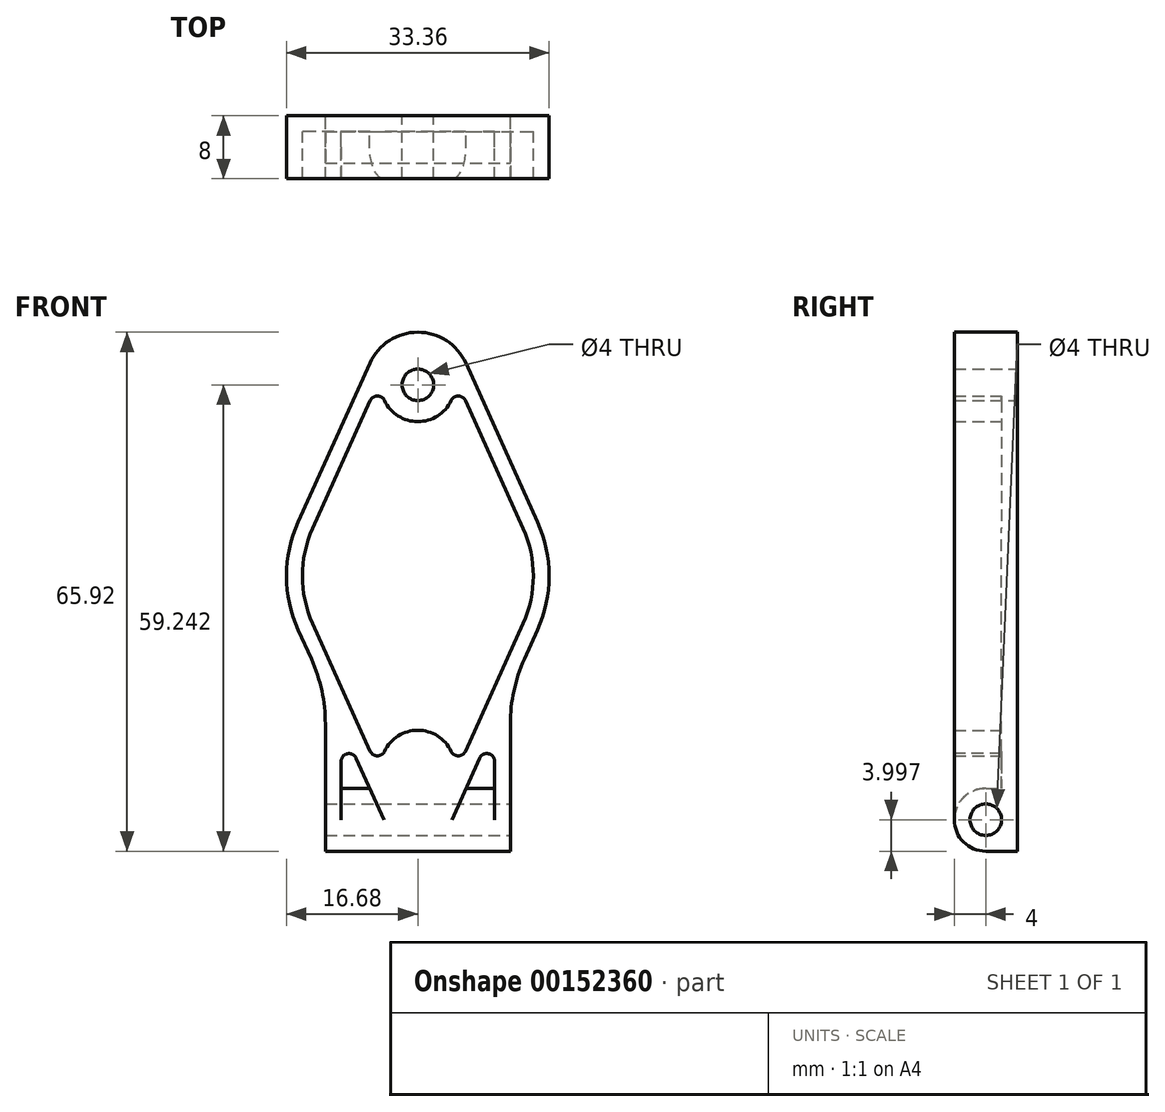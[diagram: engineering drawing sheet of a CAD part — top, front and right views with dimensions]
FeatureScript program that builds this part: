
annotation { "Feature Type Name" : "Feature", "Feature Type Description" : "" }
export const myFeature = defineFeature(function(context is Context, id is Id, definition is map)
    precondition{}
    {
        {
            var Q0;
            Q0=qCreatedBy(makeId("Front.planeOp"),FACE);
            var sketch = newSketch(context, id + "F0", { "sketchPlane" : qUnion([Q0])});
            skArc(sketch, "E0", {"start": v(6.09, 27.03) * mm, "mid": v(0, 30.96) * mm, "end": v(-6.09, 27.03) * mm});
            skArc(sketch, "E1.MirrorC", {"start": v(6.09, -27.03) * mm, "mid": v(0, -30.96) * mm, "end": v(-6.09, -27.03) * mm, "construction": true});
            skArc(sketch, "E2", {"start": v(-15.2, 6.86) * mm, "mid": v(-16.68, 0) * mm, "end": v(-15.2, -6.86) * mm});
            skLineSegment(sketch, "E3", {"start": v(-6.09, 27.03) * mm, "end": v(-15.2, 6.86) * mm});
            skLineSegment(sketch, "E4.MirrorCS", {"start": v(-6.09, -27.03) * mm, "end": v(-15.2, -6.86) * mm});
            skLineSegment(sketch, "E5.MirrorCS", {"start": v(6.09, 27.03) * mm, "end": v(15.2, 6.86) * mm});
            skLineSegment(sketch, "E6.MirrorCS", {"start": v(6.09, -27.03) * mm, "end": v(15.2, -6.86) * mm});
            skArc(sketch, "E7.trimOffspring", {"start": v(15.2, -6.86) * mm, "mid": v(16.68, 0) * mm, "end": v(15.2, 6.86) * mm});
            skCircle(sketch, "E8", {"center": v(0, 24.28) * mm, "radius": 2 * mm});
            skCircle(sketch, "E9.MirrorC", {"center": v(0, -24.28) * mm, "radius": 2 * mm});
            skLineSegment(sketch, "E10", {"start": v(-11.75, -14.5) * mm, "end": v(-11.75, -34.96) * mm});
            skLineSegment(sketch, "E11", {"start": v(-11.75, -34.96) * mm, "end": v(11.75, -34.96) * mm});
            skLineSegment(sketch, "E12", {"start": v(11.75, -34.96) * mm, "end": v(11.75, -14.5) * mm});
            skLineSegment(sketch, "E13.1", {"start": v(-6.05, 22.27) * mm, "end": v(-13.37, 6.04) * mm});
            skLineSegment(sketch, "E13.2", {"start": v(6.05, 22.27) * mm, "end": v(13.37, 6.04) * mm});
            skArc(sketch, "E13.3", {"start": v(-13.37, 6.04) * mm, "mid": v(-14.68, 0) * mm, "end": v(-13.37, -6.04) * mm});
            skArc(sketch, "E13.4", {"start": v(13.37, -6.04) * mm, "mid": v(14.68, 0) * mm, "end": v(13.37, 6.04) * mm});
            skLineSegment(sketch, "E13.5", {"start": v(6.05, -22.27) * mm, "end": v(13.37, -6.04) * mm});
            skLineSegment(sketch, "E13.7", {"start": v(-6.05, -22.27) * mm, "end": v(-13.37, -6.04) * mm});
            skLineSegment(sketch, "E14.0", {"start": v(9.75, -26.96) * mm, "end": v(9.75, -18.92) * mm});
            skLineSegment(sketch, "E14.2", {"start": v(-9.75, -18.92) * mm, "end": v(-9.75, -26.96) * mm});
            skArc(sketch, "E15", {"start": v(-4.23, 22.28) * mm, "mid": v(0, 19.6) * mm, "end": v(4.23, 22.28) * mm});
            skArc(sketch, "E16", {"start": v(4.23, -22.28) * mm, "mid": v(0, -19.6) * mm, "end": v(-4.23, -22.28) * mm});
            skPoint(sketch, "E17.visualSharp", {"position": v(-4.27, 26.2) * mm});
            skArc(sketch, "E17.filletArc", {"start": v(-4.23, 22.28) * mm, "mid": v(-5.14, 22.85) * mm, "end": v(-6.05, 22.27) * mm});
            skPoint(sketch, "E18.visualSharp", {"position": v(4.27, 26.2) * mm});
            skArc(sketch, "E18.filletArc", {"start": v(6.05, 22.27) * mm, "mid": v(5.14, 22.85) * mm, "end": v(4.23, 22.28) * mm});
            skPoint(sketch, "E19.visualSharp", {"position": v(4.27, -26.2) * mm});
            skArc(sketch, "E19.filletArc", {"start": v(4.23, -22.28) * mm, "mid": v(5.14, -22.85) * mm, "end": v(6.05, -22.27) * mm});
            skPoint(sketch, "E20.visualSharp", {"position": v(-4.27, -26.2) * mm});
            skArc(sketch, "E20.filletArc", {"start": v(-6.05, -22.27) * mm, "mid": v(-5.14, -22.85) * mm, "end": v(-4.23, -22.28) * mm});
            skLineSegment(sketch, "E21", {"start": v(-9.75, -26.96) * mm, "end": v(9.75, -26.96) * mm});
            skSolve(sketch);
        }
        {
            var Q0;
            Q0=makeQuery(id+"F0.imprint","IMPRINT",FACE,{"disambiguationData":[TD([[makeQuery(id+"F0.imprint","IMPRINT",EDGE,{"derivedFrom":sQuery(id+"F0.wireOp",EDGE,"E0")}),1.0]])]});
            var Q1;
            Q1=makeQuery(id+"F0.imprint","IMPRINT",FACE,{"disambiguationData":[TD([[makeQuery(id+"F0.imprint","IMPRINT",EDGE,{"derivedFrom":sQuery(id+"F0.wireOp",EDGE,"3e905b6d-8bee-4998-9225-6dcc00ec54d6.0")}),1.0]])]});
            var Q2;
            {var subQ0=sQuery(id+"F0.wireOp",EDGE,"E12");Q2=makeQuery(id+"F0.imprint","IMPRINT",FACE,{"disambiguationData":[TD([[makeQuery(id+"F0.imprint","IMPRINT",EDGE,{"derivedFrom":subQ0}),1.0]])]});}
            var Q3;
            {var subQ0=sQuery(id+"F0.wireOp",EDGE,"E10");Q3=makeQuery(id+"F0.imprint","IMPRINT",FACE,{"disambiguationData":[TD([[makeQuery(id+"F0.imprint","IMPRINT",EDGE,{"derivedFrom":subQ0}),1.0]])]});}
            var Q4;
            Q4=makeQuery(id+"F0.imprint","IMPRINT",FACE,{"disambiguationData":[TD([[makeQuery(id+"F0.imprint","IMPRINT",EDGE,{"derivedFrom":sQuery(id+"F0.wireOp",EDGE,"E9.MirrorC")}),1.0]])]});
            var Q5;
            Q5=makeQuery(id+"F0.imprint","IMPRINT",FACE,{"disambiguationData":[TD([[makeQuery(id+"F0.imprint","IMPRINT",EDGE,{"derivedFrom":sQuery(id+"F0.wireOp",EDGE,"E8")}),-1.0]])]});
            extrude(context, id + "F1", {"entities" : qUnion([Q0, Q1, Q2, Q3, Q4, Q5]), "depth" : 8 * mm});
        }
        {
            var Q0;
            {var subQ2=sQuery(id+"F0.wireOp",EDGE,"E13.1");Q0=makeQuery(id+"F0.imprint","IMPRINT",FACE,{"disambiguationData":[TD([[makeQuery(id+"F0.imprint","IMPRINT",EDGE,{"derivedFrom":subQ2}),1.0]])]});}
            var Q1;
            {var subQ1=sQuery(id+"F0.wireOp",EDGE,"E1.MirrorC");Q1=makeQuery(id+"F0.imprint","IMPRINT",FACE,{"disambiguationData":[TD([[makeQuery(id+"F0.imprint","IMPRINT",EDGE,{"derivedFrom":subQ1}),1.0]])]});}
            var Q2;
            {var subQ0=sQuery(id+"F0.wireOp",EDGE,"E14.2");Q2=makeQuery(id+"F0.imprint","IMPRINT",FACE,{"disambiguationData":[TD([[makeQuery(id+"F0.imprint","IMPRINT",EDGE,{"derivedFrom":subQ0}),1.0]])]});}
            var Q3;
            {var subQ0=sQuery(id+"F0.wireOp",EDGE,"E14.0");Q3=makeQuery(id+"F0.imprint","IMPRINT",FACE,{"disambiguationData":[TD([[makeQuery(id+"F0.imprint","IMPRINT",EDGE,{"derivedFrom":subQ0}),1.0]])]});}
            extrude(context, id + "F2", {"entities" : qUnion([Q0, Q1, Q2, Q3]), "operationType" : NewBodyOperationType.ADD, "depth" : 2 * mm});
        }
        {
            var Q0;
            Q0=makeQuery(id+"F1.opExtrude","SWEPT_EDGE",EDGE,{"disambiguationData":[OSD([sQuery(id+"F0.wireOp",EDGE,"E6.MirrorCS"),sQuery(id+"F0.wireOp",EDGE,"E12")])]});
            var Q1;
            Q1=makeQuery(id+"F1.opExtrude","SWEPT_EDGE",EDGE,{"disambiguationData":[OSD([sQuery(id+"F0.wireOp",EDGE,"E4.MirrorCS"),sQuery(id+"F0.wireOp",EDGE,"E10")])]});
            fillet(context, id + "F3", {"entities" : qUnion([Q0, Q1]), "radius" : 20 * mm, "tangentPropagation" : true, "allowEdgeOverflow" : false});
        }
        {
            var Q0;
            Q0=makeQuery(id+"F1.opExtrude","SWEPT_EDGE",EDGE,{"disambiguationData":[OSD([sQuery(id+"F0.wireOp",EDGE,"E6.MirrorCS"),sQuery(id+"F0.wireOp",EDGE,"E14.0")])]});
            var Q1;
            Q1=makeQuery(id+"F1.opExtrude","SWEPT_EDGE",EDGE,{"disambiguationData":[OSD([sQuery(id+"F0.wireOp",EDGE,"E4.MirrorCS"),sQuery(id+"F0.wireOp",EDGE,"E14.2")])]});
            fillet(context, id + "F4", {"entities" : qUnion([Q0, Q1]), "radius" : 1 * mm, "tangentPropagation" : true, "allowEdgeOverflow" : false});
        }
        {
            var Q0;
            Q0=makeQuery(id+"F1.opExtrude","SWEPT_FACE",FACE,{"disambiguationData":[OSD([sQuery(id+"F0.wireOp",EDGE,"E12")])]});
            var sketch = newSketch(context, id + "F5", { "sketchPlane" : qUnion([Q0])});
            skPoint(sketch, "E22", {"position": v(-4, -30.96) * mm});
            skLineSegment(sketch, "E23", {"start": v(-8, -34.96) * mm, "end": v(-4, -30.96) * mm, "construction": true});
            skLineSegment(sketch, "E24", {"start": v(-4, -30.96) * mm, "end": v(0, -34.96) * mm, "construction": true});
            skSolve(sketch);
        }
        {
            var Q0;
            Q0=sQuery(id+"F5.wireOp",VERTEX,"E22");
            var Q1;
            Q1=makeQuery(id+"F1.opExtrude","SWEPT_BODY",BODY,{"disambiguationData":[OSD([sQuery(id+"F0.wireOp",EDGE,"E0"),sQuery(id+"F0.wireOp",EDGE,"E2"),sQuery(id+"F0.wireOp",EDGE,"E3"),sQuery(id+"F0.wireOp",EDGE,"E5.MirrorCS"),sQuery(id+"F0.wireOp",EDGE,"E7.trimOffspring"),sQuery(id+"F0.wireOp",EDGE,"S2IiUO7s-7rjS-UU1n-G3Er-isHJvikYOna3"),sQuery(id+"F0.wireOp",EDGE,"U4xu2M48-wPnJ-tMoa-V4Px-PJSouQ81H8F5"),sQuery(id+"F0.wireOp",EDGE,"HV652KFt-d8Xn-WSbo-tHCJ-cfUj0g3Xd7DK"),sQuery(id+"F0.wireOp",EDGE,"E10"),sQuery(id+"F0.wireOp",EDGE,"E11"),sQuery(id+"F0.wireOp",EDGE,"E12"),sQuery(id+"F0.wireOp",EDGE,"W1IEodJy-6PRz-xiH1-2iNf-kAuRcIV7mYlj"),sQuery(id+"F0.wireOp",EDGE,"5ZKJKvnk-ET5z-qlB3-oLW5-LuLVHKlnV0HX"),sQuery(id+"F0.wireOp",EDGE,"Gk8awqwg-zgXA-VnUW-8MKI-QdblR6Wf13JX"),sQuery(id+"F0.wireOp",EDGE,"WIDdAYBM-okhh-eBsl-QBhJ-HuDdJqstO0Cl"),sQuery(id+"F0.wireOp",EDGE,"iXw4nrh7-EQqi-IiG2-VBaK-kNldmVsmUaTg"),sQuery(id+"F0.wireOp",EDGE,"03ff63bc-461f-42e4-a166-82e271801758"),sQuery(id+"F0.wireOp",EDGE,"5881da14-4dba-48e3-8e12-341ecdeeb7140.MirrorCS")])]});
            hole(context, id + "F6", {"style" : HoleStyle.SIMPLE, "endStyle" : HoleEndStyle.THROUGH, "standardTappedOrClearance" : lookupTablePath({ "standard" : "ISO", "size" : "4", "type" : "Drilled" }), "standardBlindInLast" : lookupTablePath({ "standard" : "ISO", "size" : "4", "type" : "Drilled" }), "holeDiameter" : 4 * mm, "locations" : qUnion([Q0]), "scope" : qUnion([Q1]), "isTappedThrough" : true});
        }
        {
            var Q0;
            {var subQ0=sQuery(id+"F0.wireOp",EDGE,"E11");Q0=makeQuery(id+"F1.opExtrude","CAP_EDGE",EDGE,{"disambiguationData":[OSD([subQ0]),TDD([makeQuery(id+"F0.imprint","IMPRINT",EDGE,{"disambiguationData":[TD([[makeQuery(id+"F0.imprint","INTERSECT",VERTEX,{"derivedFrom":[sQuery(id+"F0.wireOp",EDGE,"E10"),subQ0]}),-1.0]])],"derivedFrom":subQ0})])],"isStart":false});}
            var Q1;
            {var subQ0=sQuery(id+"F0.wireOp",EDGE,"E11");Q1=makeQuery(id+"F1.opExtrude","CAP_EDGE",EDGE,{"disambiguationData":[OSD([subQ0]),TDD([makeQuery(id+"F0.imprint","IMPRINT",EDGE,{"disambiguationData":[TD([[makeQuery(id+"F0.imprint","INTERSECT",VERTEX,{"derivedFrom":[subQ0,sQuery(id+"F0.wireOp",EDGE,"E12")]}),1.0]])],"derivedFrom":subQ0})])],"isStart":false});}
            var Q2;
            Q2=makeQuery(id+"F1.opExtrude","CAP_EDGE",EDGE,{"disambiguationData":[OSD([sQuery(id+"F0.wireOp",EDGE,"E21")])],"isStart":false});
            fillet(context, id + "F7", {"entities" : qUnion([Q0, Q1, Q2]), "radius" : (8 / 2) * mm, "tangentPropagation" : true, "allowEdgeOverflow" : false});
        }
    });
